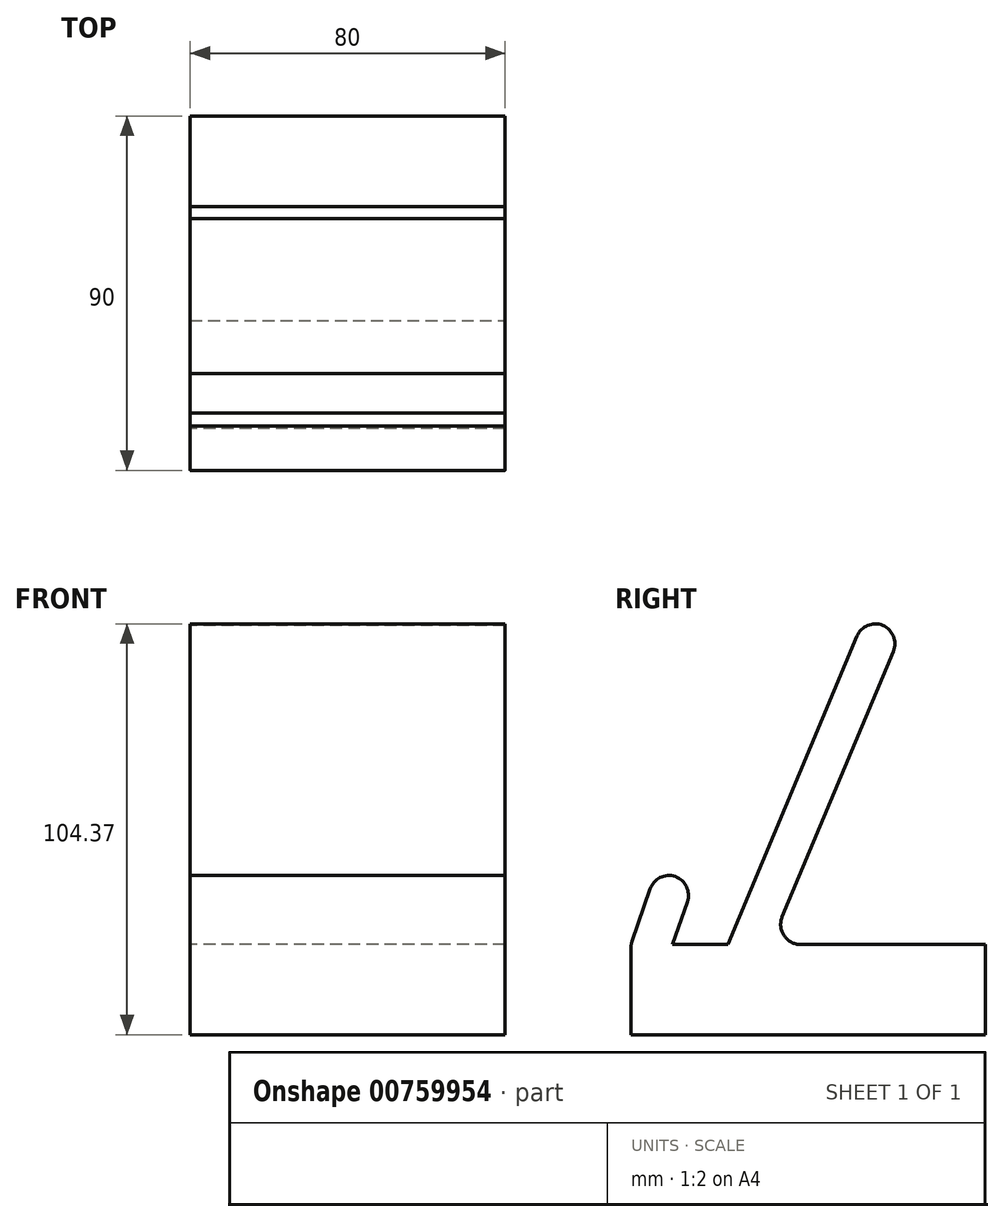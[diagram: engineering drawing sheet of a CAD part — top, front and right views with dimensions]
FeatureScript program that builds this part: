
annotation { "Feature Type Name" : "Feature", "Feature Type Description" : "" }
export const myFeature = defineFeature(function(context is Context, id is Id, definition is map)
    precondition{}
    {
        {
            var Q0;
            Q0=qCreatedBy(makeId("Right.planeOp"),FACE);
            var sketch = newSketch(context, id + "F0", { "sketchPlane" : qUnion([Q0])});
            skLineSegment(sketch, "E0.bottom", {"start": v(-71.87, -44.11) * mm, "end": v(18.13, -44.11) * mm});
            skLineSegment(sketch, "E0.top", {"start": v(-71.87, -67.02) * mm, "end": v(18.13, -67.02) * mm});
            skLineSegment(sketch, "E0.left", {"start": v(-71.87, -44.11) * mm, "end": v(-71.87, -67.02) * mm});
            skLineSegment(sketch, "E0.right", {"start": v(18.13, -44.11) * mm, "end": v(18.13, -67.02) * mm});
            skLineSegment(sketch, "E1", {"start": v(-71.87, -44.11) * mm, "end": v(-65.37, -25.2) * mm});
            skLineSegment(sketch, "E2", {"start": v(-65.37, -25.2) * mm, "end": v(-55.91, -28.45) * mm});
            skLineSegment(sketch, "E3", {"start": v(-55.91, -28.45) * mm, "end": v(-61.3, -44.11) * mm});
            skLineSegment(sketch, "E4", {"start": v(-47.25, -44.03) * mm, "end": v(-47.25, -44.11) * mm});
            skLineSegment(sketch, "E5", {"start": v(-47.25, -44.11) * mm, "end": v(-12.52, 38.92) * mm});
            skPoint(sketch, "E5.startSnap0", {"position": v(-47.25, -44.03) * mm});
            skLineSegment(sketch, "E6", {"start": v(-12.52, 38.92) * mm, "end": v(-3.3, 35.06) * mm});
            skLineSegment(sketch, "E7", {"start": v(-3.3, 35.06) * mm, "end": v(-36.4, -44.11) * mm});
            skLineSegment(sketch, "E8", {"start": v(-47.08, -44.11) * mm, "end": v(-47.25, -44.03) * mm});
            skPoint(sketch, "E9.orphan", {"position": v(-47.25, -41.07) * mm});
            skPoint(sketch, "E10.orphan", {"position": v(-47.25, -47) * mm});
            skSolve(sketch);
        }
        {
            var Q0;
            Q0 = qSketchRegion(id + "F0", true);
            extrude(context, id + "F1", {"entities" : qUnion([Q0]), "depth" : 80 * mm, "offsetDistance" : 25.4 * mm});
        }
        {
            var Q0;
            Q0=makeQuery(id+"F1.opExtrude","SWEPT_EDGE",EDGE,{"disambiguationData":[OSD([sQuery(id+"F0.wireOp",EDGE,"E0.bottom"),sQuery(id+"F0.wireOp",EDGE,"E0.left"),sQuery(id+"F0.wireOp",EDGE,"E1")])]});
            fillet(context, id + "F2", {"entities" : qUnion([Q0]), "radius" : 5 * mm, "tangentPropagation" : true, "allowEdgeOverflow" : false});
        }
        {
            var Q0;
            Q0=makeQuery(id+"F1.opExtrude","SWEPT_EDGE",EDGE,{"disambiguationData":[OSD([sQuery(id+"F0.wireOp",EDGE,"E6"),sQuery(id+"F0.wireOp",EDGE,"E7")])]});
            var Q1;
            Q1=makeQuery(id+"F1.opExtrude","SWEPT_EDGE",EDGE,{"disambiguationData":[OSD([sQuery(id+"F0.wireOp",EDGE,"E5"),sQuery(id+"F0.wireOp",EDGE,"E6")])]});
            fillet(context, id + "F3", {"entities" : qUnion([Q0, Q1]), "radius" : 5.08 * mm, "tangentPropagation" : true, "allowEdgeOverflow" : false});
        }
        {
            var Q0;
            Q0=makeQuery(id+"F1.opExtrude","SWEPT_EDGE",EDGE,{"disambiguationData":[OSD([sQuery(id+"F0.wireOp",EDGE,"E2"),sQuery(id+"F0.wireOp",EDGE,"E3")])]});
            var Q1;
            Q1=makeQuery(id+"F1.opExtrude","SWEPT_EDGE",EDGE,{"disambiguationData":[OSD([sQuery(id+"F0.wireOp",EDGE,"E1"),sQuery(id+"F0.wireOp",EDGE,"E2")])]});
            fillet(context, id + "F4", {"entities" : qUnion([Q0, Q1]), "radius" : 5.08 * mm, "tangentPropagation" : true, "allowEdgeOverflow" : false});
        }
        {
            var Q0;
            Q0=makeQuery(id+"F1.opExtrude","SWEPT_EDGE",EDGE,{"disambiguationData":[OSD([sQuery(id+"F0.wireOp",EDGE,"E0.bottom"),sQuery(id+"F0.wireOp",EDGE,"E7")])]});
            fillet(context, id + "F5", {"entities" : qUnion([Q0]), "radius" : 5.08 * mm, "tangentPropagation" : true, "allowEdgeOverflow" : false});
        }
    });
